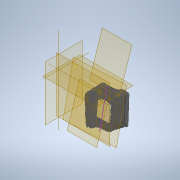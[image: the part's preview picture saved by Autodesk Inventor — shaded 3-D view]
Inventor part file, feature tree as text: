
AUTODESK INVENTOR PART (.ipt)
format: ipt  version: 2021 (Build 250183000, 183)  size: 522,752 bytes
history: native  units: mm
features: plane x3, other x2, sketch x2, extrude x1
ambient origin geometry x8: Origin, YZ Plane, XZ Plane, XY Plane, X Axis, Y Axis, Z Axis, Center Point
bodies: Solid1 (feature_tree)
feature tree (8):
  other  "WaveRunnerFootPedal"
  plane  "Work Plane2"
  sketch  "Sketch1"  dims[d0=-3.141593mm d1=-210.0mm d2=1.22173mm]
  plane  "Work Plane3"
  extrude  "Extrusion1"  Depth=1.22173mm
  plane  "Work Plane1"
  sketch  "Sketch2"  dims[d3=67.25mm d4=0.0mm]
  other  "MeshFeature1"
